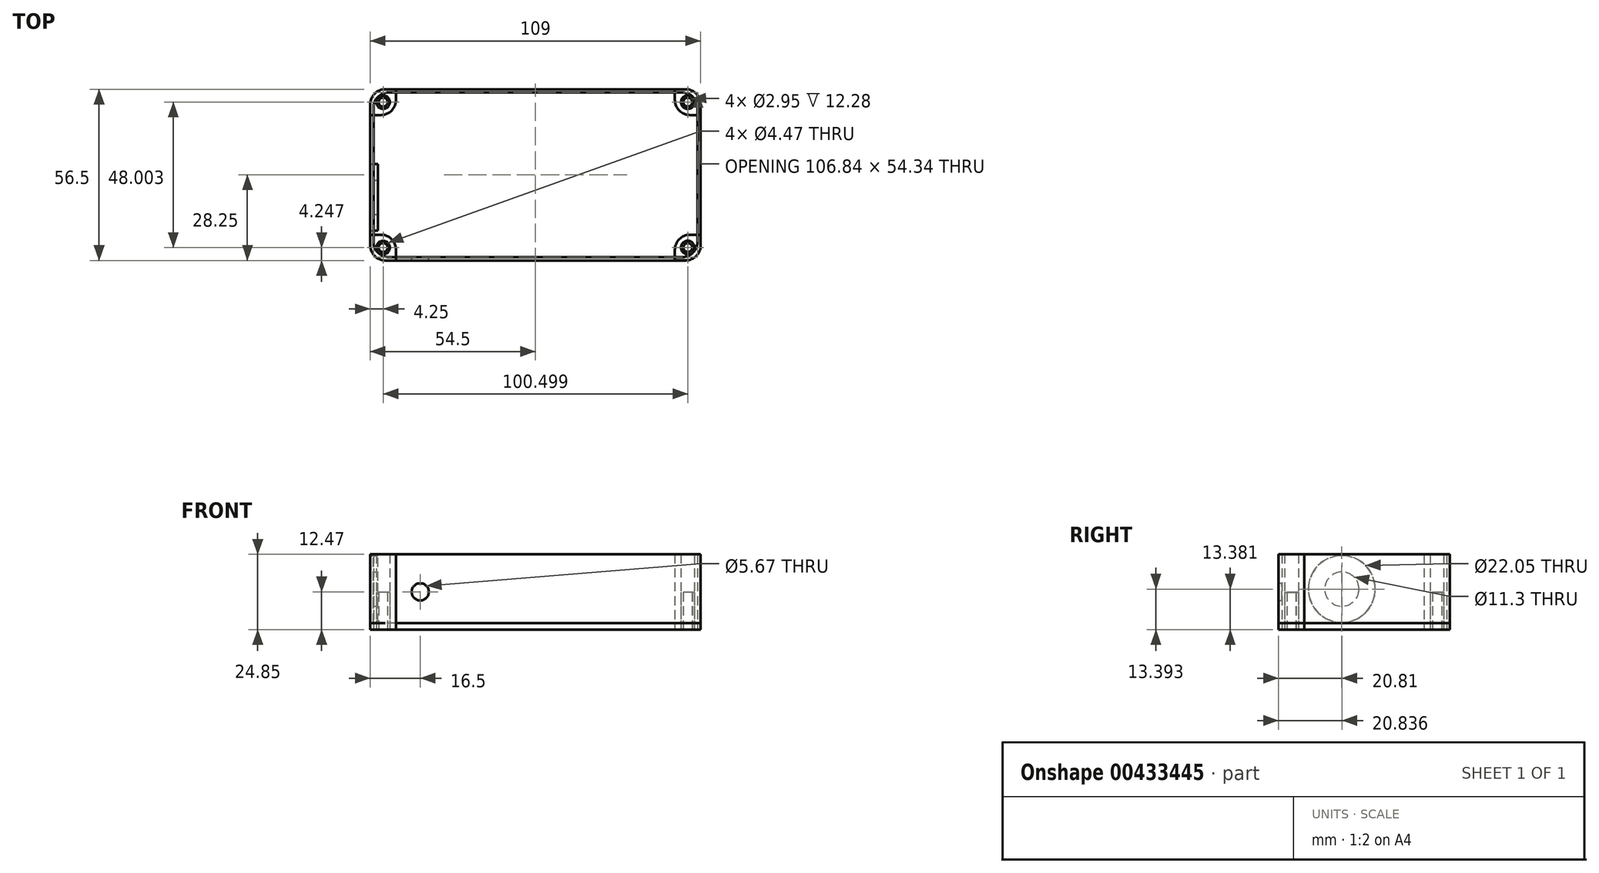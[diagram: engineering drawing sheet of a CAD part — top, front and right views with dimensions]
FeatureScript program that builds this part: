
annotation { "Feature Type Name" : "Feature", "Feature Type Description" : "" }
export const myFeature = defineFeature(function(context is Context, id is Id, definition is map)
    precondition{}
    {
        {
            var Q0;
            Q0=qCreatedBy(makeId("Top.planeOp"),FACE);
            var sketch = newSketch(context, id + "F0", { "sketchPlane" : qUnion([Q0])});
            skLineSegment(sketch, "E0.bottom", {"start": v(49.5, -28.25) * mm, "end": v(-49.5, -28.25) * mm});
            skLineSegment(sketch, "E0.top", {"start": v(49.5, 28.25) * mm, "end": v(-49.5, 28.25) * mm});
            skLineSegment(sketch, "E0.left", {"start": v(54.5, -23.25) * mm, "end": v(54.5, 23.25) * mm});
            skLineSegment(sketch, "E0.right", {"start": v(-54.5, -23.25) * mm, "end": v(-54.5, 23.25) * mm});
            skPoint(sketch, "E0.middle", {"position": v(0, 0) * mm});
            skPoint(sketch, "E1.visualSharp", {"position": v(-54.5, 28.25) * mm});
            skArc(sketch, "E1.filletArc", {"start": v(-49.5, 28.25) * mm, "mid": v(-53.04, 26.79) * mm, "end": v(-54.5, 23.25) * mm});
            skPoint(sketch, "E2.visualSharp", {"position": v(-53.42, 27.17) * mm});
            skPoint(sketch, "E3.visualSharp", {"position": v(-53.42, -27.17) * mm});
            skPoint(sketch, "E4.visualSharp", {"position": v(53.42, -27.17) * mm});
            skPoint(sketch, "E5.visualSharp", {"position": v(53.42, 27.17) * mm});
            skPoint(sketch, "E6.visualSharp", {"position": v(54.5, 28.25) * mm});
            skArc(sketch, "E6.filletArc", {"start": v(54.5, 23.25) * mm, "mid": v(53.04, 26.79) * mm, "end": v(49.5, 28.25) * mm});
            skPoint(sketch, "E7.visualSharp", {"position": v(54.5, -28.25) * mm});
            skArc(sketch, "E7.filletArc", {"start": v(49.5, -28.25) * mm, "mid": v(53.04, -26.79) * mm, "end": v(54.5, -23.25) * mm});
            skPoint(sketch, "E8.visualSharp", {"position": v(-54.5, -28.25) * mm});
            skArc(sketch, "E8.filletArc", {"start": v(-54.5, -23.25) * mm, "mid": v(-53.04, -26.79) * mm, "end": v(-49.5, -28.25) * mm});
            skSolve(sketch);
        }
        {
            var Q0;
            Q0=makeQuery(id+"F0.imprint","IMPRINT",FACE,{"disambiguationData":[TD([[makeQuery(id+"F0.imprint","IMPRINT",EDGE,{"derivedFrom":sQuery(id+"F0.wireOp",EDGE,"E0.bottom")}),-1.0]])]});
            extrude(context, id + "F1", {"entities" : qUnion([Q0]), "depth" : 2.16 * mm});
        }
        {
            var Q0;
            Q0=qCreatedBy(makeId("Top.planeOp"),FACE);
            var sketch = newSketch(context, id + "F2", { "sketchPlane" : qUnion([Q0])});
            skLineSegment(sketch, "E9.bottom", {"start": v(49.5, -28.25) * mm, "end": v(-49.5, -28.25) * mm});
            skLineSegment(sketch, "E9.top", {"start": v(49.5, 28.25) * mm, "end": v(-49.5, 28.25) * mm});
            skLineSegment(sketch, "E9.left", {"start": v(54.5, -23.25) * mm, "end": v(54.5, 23.25) * mm});
            skLineSegment(sketch, "E9.right", {"start": v(-54.5, -23.25) * mm, "end": v(-54.5, 23.25) * mm});
            skPoint(sketch, "E9.middle", {"position": v(0, 0) * mm});
            skPoint(sketch, "E10.visualSharp", {"position": v(-54.5, 28.25) * mm});
            skArc(sketch, "E10.filletArc", {"start": v(-49.5, 28.25) * mm, "mid": v(-53.04, 26.79) * mm, "end": v(-54.5, 23.25) * mm});
            skPoint(sketch, "E11.visualSharp", {"position": v(-53.42, 27.17) * mm});
            skPoint(sketch, "E12.visualSharp", {"position": v(-53.42, -27.17) * mm});
            skPoint(sketch, "E13.visualSharp", {"position": v(53.42, -27.17) * mm});
            skPoint(sketch, "E14.visualSharp", {"position": v(53.42, 27.17) * mm});
            skPoint(sketch, "E15.visualSharp", {"position": v(54.5, 28.25) * mm});
            skArc(sketch, "E15.filletArc", {"start": v(54.5, 23.25) * mm, "mid": v(53.04, 26.79) * mm, "end": v(49.5, 28.25) * mm});
            skPoint(sketch, "E16.visualSharp", {"position": v(54.5, -28.25) * mm});
            skArc(sketch, "E16.filletArc", {"start": v(49.5, -28.25) * mm, "mid": v(53.04, -26.79) * mm, "end": v(54.5, -23.25) * mm});
            skPoint(sketch, "E17.visualSharp", {"position": v(-54.5, -28.25) * mm});
            skArc(sketch, "E17.filletArc", {"start": v(-54.5, -23.25) * mm, "mid": v(-53.04, -26.79) * mm, "end": v(-49.5, -28.25) * mm});
            skLineSegment(sketch, "E18.bottom", {"start": v(48.42, 27.17) * mm, "end": v(-48.42, 27.17) * mm});
            skLineSegment(sketch, "E18.top", {"start": v(48.42, -27.17) * mm, "end": v(-48.42, -27.17) * mm});
            skLineSegment(sketch, "E18.left", {"start": v(53.42, 22.17) * mm, "end": v(53.42, -22.17) * mm});
            skLineSegment(sketch, "E18.right", {"start": v(-53.42, 22.17) * mm, "end": v(-53.42, -22.17) * mm});
            skArc(sketch, "E19.filletArc", {"start": v(-48.42, 27.17) * mm, "mid": v(-51.96, 25.7) * mm, "end": v(-53.42, 22.17) * mm});
            skArc(sketch, "E20.filletArc", {"start": v(-53.42, -22.17) * mm, "mid": v(-51.96, -25.7) * mm, "end": v(-48.42, -27.17) * mm});
            skArc(sketch, "E21.filletArc", {"start": v(48.42, -27.17) * mm, "mid": v(51.96, -25.7) * mm, "end": v(53.42, -22.17) * mm});
            skArc(sketch, "E22.filletArc", {"start": v(53.42, 22.17) * mm, "mid": v(51.96, 25.7) * mm, "end": v(48.42, 27.17) * mm});
            skSolve(sketch);
        }
        {
            var Q0;
            Q0=makeQuery(id+"F2.imprint","IMPRINT",FACE,{"disambiguationData":[TD([[makeQuery(id+"F2.imprint","IMPRINT",EDGE,{"derivedFrom":sQuery(id+"F2.wireOp",EDGE,"E9.bottom")}),-1.0]])]});
            extrude(context, id + "F3", {"entities" : qUnion([Q0]), "depth" : 24.85 * mm});
        }
        {
            var Q0;
            Q0=qCreatedBy(makeId("Top.planeOp"),FACE);
            var sketch = newSketch(context, id + "F4", { "sketchPlane" : qUnion([Q0])});
            skLineSegment(sketch, "E23.bottom", {"start": v(-51, 19.75) * mm, "end": v(-54.5, 19.75) * mm});
            skLineSegment(sketch, "E23.top", {"start": v(-46, 28.25) * mm, "end": v(-49.5, 28.25) * mm});
            skLineSegment(sketch, "E23.left", {"start": v(-46, 24.75) * mm, "end": v(-46, 28.25) * mm});
            skLineSegment(sketch, "E23.right", {"start": v(-54.5, 19.75) * mm, "end": v(-54.5, 23.25) * mm});
            skPoint(sketch, "E23.middle", {"position": v(-50.24, 24) * mm});
            skCircle(sketch, "E24", {"center": v(-50.24, 24) * mm, "radius": 2.24 * mm});
            skLineSegment(sketch, "E25.bottom", {"start": v(49.5, -28.25) * mm, "end": v(46, -28.25) * mm});
            skLineSegment(sketch, "E25.top", {"start": v(54.5, -19.75) * mm, "end": v(51, -19.75) * mm});
            skLineSegment(sketch, "E25.left", {"start": v(54.5, -23.25) * mm, "end": v(54.5, -19.75) * mm});
            skLineSegment(sketch, "E25.right", {"start": v(46, -28.25) * mm, "end": v(46, -24.75) * mm});
            skPoint(sketch, "E25.middle", {"position": v(50.25, -24) * mm});
            skCircle(sketch, "E26", {"center": v(50.25, -24) * mm, "radius": 2.24 * mm});
            skLineSegment(sketch, "E27.bottom", {"start": v(54.5, 19.75) * mm, "end": v(51, 19.75) * mm});
            skLineSegment(sketch, "E27.top", {"start": v(49.5, 28.25) * mm, "end": v(46, 28.25) * mm});
            skLineSegment(sketch, "E27.left", {"start": v(54.5, 19.75) * mm, "end": v(54.5, 23.25) * mm});
            skLineSegment(sketch, "E27.right", {"start": v(46, 24.75) * mm, "end": v(46, 28.25) * mm});
            skPoint(sketch, "E27.middle", {"position": v(50.24, 24) * mm});
            skCircle(sketch, "E28", {"center": v(50.24, 24) * mm, "radius": 2.24 * mm});
            skLineSegment(sketch, "E29.bottom", {"start": v(-46, -28.25) * mm, "end": v(-49.5, -28.25) * mm});
            skLineSegment(sketch, "E29.top", {"start": v(-51, -19.75) * mm, "end": v(-54.5, -19.75) * mm});
            skLineSegment(sketch, "E29.left", {"start": v(-46, -28.25) * mm, "end": v(-46, -24.75) * mm});
            skLineSegment(sketch, "E29.right", {"start": v(-54.5, -23.25) * mm, "end": v(-54.5, -19.75) * mm});
            skPoint(sketch, "E29.middle", {"position": v(-50.25, -24) * mm});
            skCircle(sketch, "E30", {"center": v(-50.25, -24) * mm, "radius": 2.24 * mm});
            skPoint(sketch, "E31.visualSharp", {"position": v(54.5, -28.25) * mm});
            skArc(sketch, "E31.filletArc", {"start": v(49.5, -28.25) * mm, "mid": v(53.03, -26.78) * mm, "end": v(54.5, -23.25) * mm});
            skPoint(sketch, "E32.visualSharp", {"position": v(46, -19.75) * mm});
            skArc(sketch, "E32.filletArc", {"start": v(51, -19.75) * mm, "mid": v(47.46, -21.21) * mm, "end": v(46, -24.75) * mm});
            skPoint(sketch, "E33.visualSharp", {"position": v(54.5, 28.25) * mm});
            skArc(sketch, "E33.filletArc", {"start": v(54.5, 23.25) * mm, "mid": v(53.03, 26.79) * mm, "end": v(49.5, 28.25) * mm});
            skPoint(sketch, "E34.visualSharp", {"position": v(46, 19.75) * mm});
            skArc(sketch, "E34.filletArc", {"start": v(46, 24.75) * mm, "mid": v(47.46, 21.21) * mm, "end": v(51, 19.75) * mm});
            skPoint(sketch, "E35.visualSharp", {"position": v(-46, 19.75) * mm});
            skArc(sketch, "E35.filletArc", {"start": v(-51, 19.75) * mm, "mid": v(-47.46, 21.21) * mm, "end": v(-46, 24.75) * mm});
            skPoint(sketch, "E36.visualSharp", {"position": v(-54.5, 28.25) * mm});
            skArc(sketch, "E36.filletArc", {"start": v(-49.5, 28.25) * mm, "mid": v(-53.03, 26.78) * mm, "end": v(-54.5, 23.25) * mm});
            skPoint(sketch, "E37.visualSharp", {"position": v(-54.5, -28.25) * mm});
            skArc(sketch, "E37.filletArc", {"start": v(-54.5, -23.25) * mm, "mid": v(-53.04, -26.79) * mm, "end": v(-49.5, -28.25) * mm});
            skPoint(sketch, "E38.visualSharp", {"position": v(-46, -19.75) * mm});
            skArc(sketch, "E38.filletArc", {"start": v(-46, -24.75) * mm, "mid": v(-47.46, -21.22) * mm, "end": v(-51, -19.75) * mm});
            skSolve(sketch);
        }
        {
            var Q0;
            Q0=makeQuery(id+"F4.imprint","IMPRINT",FACE,{"disambiguationData":[TD([[makeQuery(id+"F4.imprint","IMPRINT",EDGE,{"derivedFrom":sQuery(id+"F4.wireOp",EDGE,"E25.bottom")}),-1.0]])]});
            var Q1;
            Q1=makeQuery(id+"F4.imprint","IMPRINT",FACE,{"disambiguationData":[TD([[makeQuery(id+"F4.imprint","IMPRINT",EDGE,{"derivedFrom":sQuery(id+"F4.wireOp",EDGE,"E27.bottom")}),-1.0]])]});
            var Q2;
            Q2=makeQuery(id+"F4.imprint","IMPRINT",FACE,{"disambiguationData":[TD([[makeQuery(id+"F4.imprint","IMPRINT",EDGE,{"derivedFrom":sQuery(id+"F4.wireOp",EDGE,"E29.bottom")}),-1.0]])]});
            var Q3;
            Q3=makeQuery(id+"F4.imprint","IMPRINT",FACE,{"disambiguationData":[TD([[makeQuery(id+"F4.imprint","IMPRINT",EDGE,{"derivedFrom":sQuery(id+"F4.wireOp",EDGE,"E23.bottom")}),-1.0]])]});
            extrude(context, id + "F5", {"entities" : qUnion([Q0, Q1, Q2, Q3]), "depth" : 24.85 * mm});
        }
        {
            var Q0;
            Q0=qCreatedBy(makeId("Top.planeOp"),FACE);
            var sketch = newSketch(context, id + "F6", { "sketchPlane" : qUnion([Q0])});
            skPoint(sketch, "E39.middle", {"position": v(-50.24, 24) * mm});
            skCircle(sketch, "E40", {"center": v(-50.24, 24) * mm, "radius": 2.24 * mm});
            skPoint(sketch, "E41.middle", {"position": v(50.25, -24) * mm});
            skCircle(sketch, "E42", {"center": v(50.25, -24) * mm, "radius": 2.24 * mm});
            skPoint(sketch, "E43.middle", {"position": v(50.24, 24) * mm});
            skCircle(sketch, "E44", {"center": v(50.24, 24) * mm, "radius": 2.24 * mm});
            skPoint(sketch, "E45.middle", {"position": v(-50.25, -24) * mm});
            skCircle(sketch, "E46", {"center": v(-50.25, -24) * mm, "radius": 2.24 * mm});
            skCircle(sketch, "E47", {"center": v(-50.24, 24) * mm, "radius": 1.47 * mm});
            skCircle(sketch, "E48", {"center": v(-50.25, -24) * mm, "radius": 1.47 * mm});
            skCircle(sketch, "E49", {"center": v(50.25, -24) * mm, "radius": 1.47 * mm});
            skCircle(sketch, "E50", {"center": v(50.24, 24) * mm, "radius": 1.47 * mm});
            skSolve(sketch);
        }
        {
            var Q0;
            Q0=makeQuery(id+"F6.imprint","IMPRINT",FACE,{"disambiguationData":[TD([[makeQuery(id+"F6.imprint","IMPRINT",EDGE,{"derivedFrom":sQuery(id+"F6.wireOp",EDGE,"E40")}),1.0]])]});
            var Q1;
            Q1=makeQuery(id+"F6.imprint","IMPRINT",FACE,{"disambiguationData":[TD([[makeQuery(id+"F6.imprint","IMPRINT",EDGE,{"derivedFrom":sQuery(id+"F6.wireOp",EDGE,"E44")}),1.0]])]});
            var Q2;
            Q2=makeQuery(id+"F6.imprint","IMPRINT",FACE,{"disambiguationData":[TD([[makeQuery(id+"F6.imprint","IMPRINT",EDGE,{"derivedFrom":sQuery(id+"F6.wireOp",EDGE,"E42")}),1.0]])]});
            var Q3;
            Q3=makeQuery(id+"F6.imprint","IMPRINT",FACE,{"disambiguationData":[TD([[makeQuery(id+"F6.imprint","IMPRINT",EDGE,{"derivedFrom":sQuery(id+"F6.wireOp",EDGE,"E46")}),1.0]])]});
            extrude(context, id + "F7", {"entities" : qUnion([Q0, Q1, Q2, Q3]), "depth" : 12.28 * mm});
        }
        {
            var Q0;
            Q0=qCreatedBy(makeId("Front.planeOp"),FACE);
            var sketch = newSketch(context, id + "F8", { "sketchPlane" : qUnion([Q0])});
            skCircle(sketch, "E51", {"center": v(-38, 12.47) * mm, "radius": 2.83 * mm});
            skSolve(sketch);
        }
        {
            var Q0;
            Q0=sQuery(id+"F8.wireOp",VERTEX,"E51.center");
            var Q1;
            Q1=makeQuery(id+"F3.opExtrude","SWEPT_BODY",BODY,{"disambiguationData":[OSD([sQuery(id+"F2.wireOp",EDGE,"E9.bottom"),sQuery(id+"F2.wireOp",EDGE,"E9.top"),sQuery(id+"F2.wireOp",EDGE,"E9.left"),sQuery(id+"F2.wireOp",EDGE,"E9.right"),sQuery(id+"F2.wireOp",EDGE,"E10.filletArc"),sQuery(id+"F2.wireOp",EDGE,"E15.filletArc"),sQuery(id+"F2.wireOp",EDGE,"E16.filletArc"),sQuery(id+"F2.wireOp",EDGE,"E17.filletArc"),sQuery(id+"F2.wireOp",EDGE,"E18.bottom"),sQuery(id+"F2.wireOp",EDGE,"E18.top"),sQuery(id+"F2.wireOp",EDGE,"E18.left"),sQuery(id+"F2.wireOp",EDGE,"E18.right"),sQuery(id+"F2.wireOp",EDGE,"E19.filletArc"),sQuery(id+"F2.wireOp",EDGE,"E20.filletArc"),sQuery(id+"F2.wireOp",EDGE,"E21.filletArc"),sQuery(id+"F2.wireOp",EDGE,"E22.filletArc")])]});
            hole(context, id + "F9", {"style" : HoleStyle.SIMPLE, "endStyle" : HoleEndStyle.THROUGH, "oppositeDirection" : true, "holeDiameter" : 5.67 * mm, "isTappedThrough" : true, "tappedDepth" : 12 * mm, "tapClearance" : 3, "locations" : qUnion([Q0]), "scope" : qUnion([Q1])});
        }
        {
            var Q0;
            Q0=qCreatedBy(makeId("Right.planeOp"),FACE);
            var sketch = newSketch(context, id + "F10", { "sketchPlane" : qUnion([Q0])});
            skCircle(sketch, "E52", {"center": v(-7.44, 13.4) * mm, "radius": 11.03 * mm});
            skSolve(sketch);
        }
        {
            var Q0;
            Q0=sQuery(id+"F10.wireOp",VERTEX,"E52.center");
            var Q1;
            Q1=makeQuery(id+"F3.opExtrude","SWEPT_BODY",BODY,{"disambiguationData":[OSD([sQuery(id+"F2.wireOp",EDGE,"E9.bottom"),sQuery(id+"F2.wireOp",EDGE,"E9.top"),sQuery(id+"F2.wireOp",EDGE,"E9.left"),sQuery(id+"F2.wireOp",EDGE,"E9.right"),sQuery(id+"F2.wireOp",EDGE,"E10.filletArc"),sQuery(id+"F2.wireOp",EDGE,"E15.filletArc"),sQuery(id+"F2.wireOp",EDGE,"E16.filletArc"),sQuery(id+"F2.wireOp",EDGE,"E17.filletArc"),sQuery(id+"F2.wireOp",EDGE,"E18.bottom"),sQuery(id+"F2.wireOp",EDGE,"E18.top"),sQuery(id+"F2.wireOp",EDGE,"E18.left"),sQuery(id+"F2.wireOp",EDGE,"E18.right"),sQuery(id+"F2.wireOp",EDGE,"E19.filletArc"),sQuery(id+"F2.wireOp",EDGE,"E20.filletArc"),sQuery(id+"F2.wireOp",EDGE,"E21.filletArc"),sQuery(id+"F2.wireOp",EDGE,"E22.filletArc")])]});
            hole(context, id + "F11", {"style" : HoleStyle.SIMPLE, "endStyle" : HoleEndStyle.THROUGH, "holeDiameter" : 22.05 * mm, "isTappedThrough" : true, "tappedDepth" : 12 * mm, "tapClearance" : 3, "locations" : qUnion([Q0]), "scope" : qUnion([Q1])});
        }
        {
            var Q0;
            Q0=qCreatedBy(makeId("Right.planeOp"),FACE);
            var sketch = newSketch(context, id + "F12", { "sketchPlane" : qUnion([Q0])});
            skCircle(sketch, "E53", {"center": v(-7.41, 13.38) * mm, "radius": 11.03 * mm});
            skCircle(sketch, "E54", {"center": v(-7.41, 13.38) * mm, "radius": 5.65 * mm});
            skSolve(sketch);
        }
        {
            var Q0;
            Q0=makeQuery(id+"F12.imprint","IMPRINT",FACE,{"disambiguationData":[TD([[makeQuery(id+"F12.imprint","IMPRINT",EDGE,{"derivedFrom":sQuery(id+"F12.wireOp",EDGE,"E53")}),1.0]])]});
            extrude(context, id + "F13", {"entities" : qUnion([Q0]), "oppositeDirection" : true, "depth" : 1.5 * mm});
        }
        {
            var Q0;
            Q0=makeQuery(id+"F13.opExtrude","SWEPT_BODY",BODY,{"disambiguationData":[OSD([sQuery(id+"F12.wireOp",EDGE,"E53"),sQuery(id+"F12.wireOp",EDGE,"E54")])]});
            transform(context, id + "F14", {"entities" : qUnion([Q0]), "transformType" : TransformType.TRANSLATION_3D, "dx" : -52 * mm, "dy" : 0 * mm, "dz" : 0 * mm, "makeCopy" : false});
        }
    });
